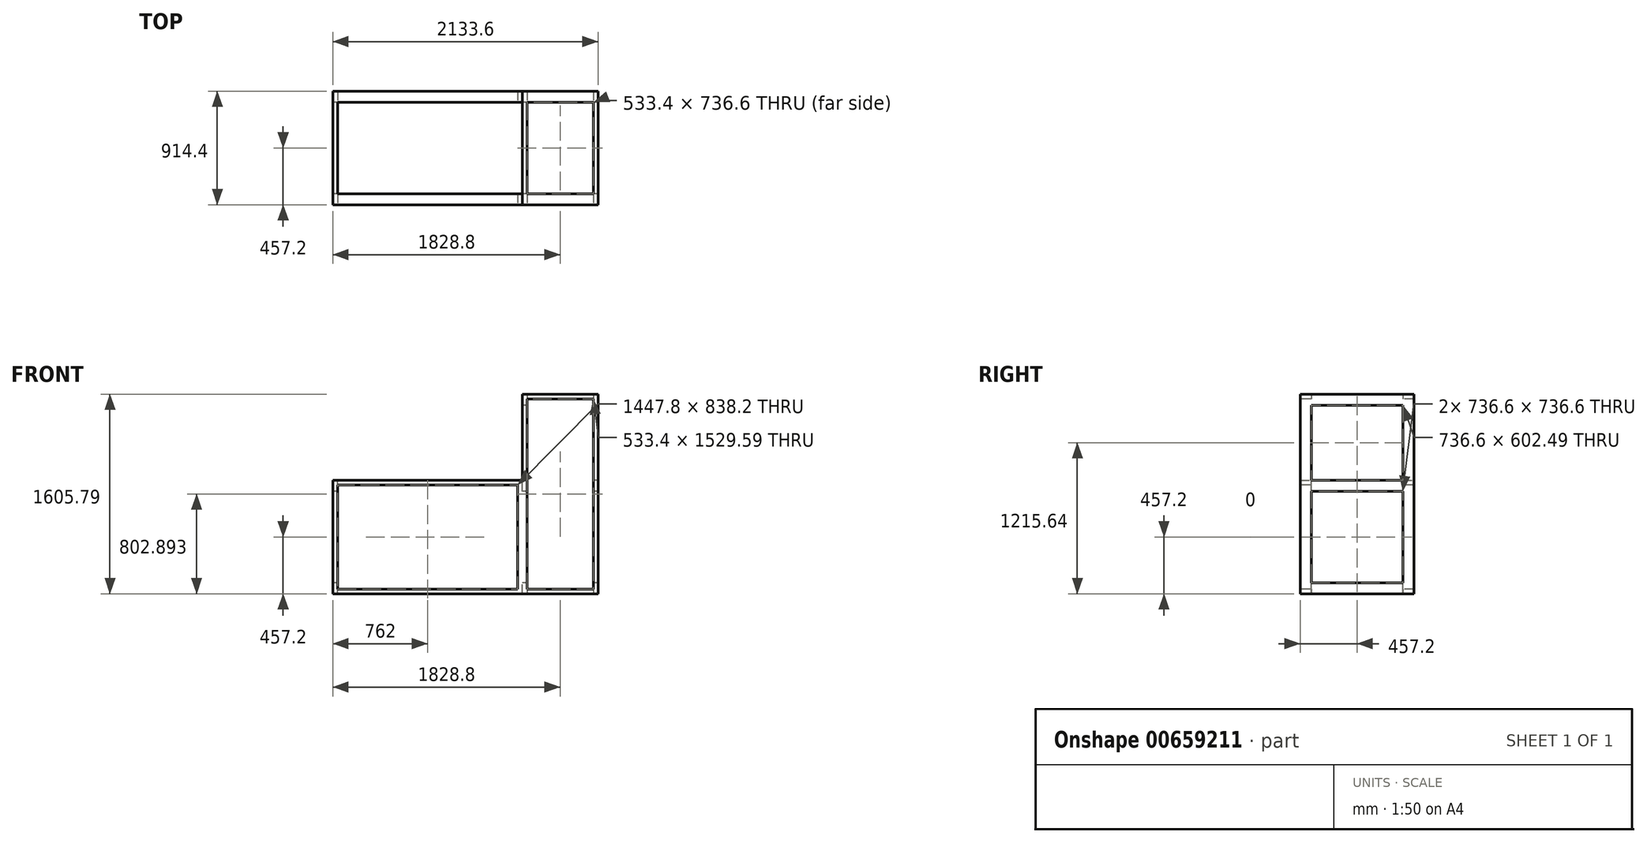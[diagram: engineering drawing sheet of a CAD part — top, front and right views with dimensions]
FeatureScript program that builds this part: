
annotation { "Feature Type Name" : "Feature", "Feature Type Description" : "" }
export const myFeature = defineFeature(function(context is Context, id is Id, definition is map)
    precondition{}
    {
        {
            var Q0;
            Q0=qCreatedBy(makeId("Front.planeOp"),FACE);
            var sketch = newSketch(context, id + "F0", { "sketchPlane" : qUnion([Q0])});
            skLineSegment(sketch, "E0.bottom", {"start": v(762, 457.2) * mm, "end": v(-762, 457.2) * mm});
            skLineSegment(sketch, "E0.top", {"start": v(762, -457.2) * mm, "end": v(-762, -457.2) * mm});
            skLineSegment(sketch, "E0.left", {"start": v(762, 457.2) * mm, "end": v(762, -457.2) * mm});
            skLineSegment(sketch, "E0.right", {"start": v(-762, 457.2) * mm, "end": v(-762, -457.2) * mm});
            skPoint(sketch, "E0.middle", {"position": v(0, 0) * mm});
            skLineSegment(sketch, "E1.bottom", {"start": v(762, -457.2) * mm, "end": v(1371.6, -457.2) * mm});
            skLineSegment(sketch, "E1.top", {"start": v(762, 1148.59) * mm, "end": v(1371.6, 1148.59) * mm});
            skLineSegment(sketch, "E1.left", {"start": v(762, -457.2) * mm, "end": v(762, 1148.59) * mm});
            skLineSegment(sketch, "E1.right", {"start": v(1371.6, -457.2) * mm, "end": v(1371.6, 1148.59) * mm});
            skSolve(sketch);
        }
        {
            var Q0;
            Q0 = qSketchRegion(id + "F0", true);
            extrude(context, id + "F1", {"entities" : qUnion([Q0]), "endBound" : BoundingType.SYMMETRIC, "depth" : 914.4 * mm, "offsetDistance" : 25.4 * mm});
        }
        {
            var Q0;
            Q0=makeQuery(id+"F1.opExtrude","SWEPT_FACE",FACE,{"disambiguationData":[OSD([sQuery(id+"F0.wireOp",EDGE,"E0.right")])]});
            var sketch = newSketch(context, id + "F2", { "sketchPlane" : qUnion([Q0])});
            skLineSegment(sketch, "E2.bottom", {"start": v(368.3, 368.3) * mm, "end": v(-368.3, 368.3) * mm});
            skLineSegment(sketch, "E2.top", {"start": v(368.3, -368.3) * mm, "end": v(-368.3, -368.3) * mm});
            skLineSegment(sketch, "E2.left", {"start": v(368.3, 368.3) * mm, "end": v(368.3, -368.3) * mm});
            skLineSegment(sketch, "E2.right", {"start": v(-368.3, 368.3) * mm, "end": v(-368.3, -368.3) * mm});
            skPoint(sketch, "E2.middle", {"position": v(0, 0) * mm});
            skSolve(sketch);
        }
        {
            var Q0;
            Q0 = qSketchRegion(id + "F2", true);
            extrude(context, id + "F3", {"entities" : qUnion([Q0]), "operationType" : NewBodyOperationType.REMOVE, "endBound" : BoundingType.UP_TO_NEXT, "oppositeDirection" : true, "depth" : 25.4 * mm, "offsetDistance" : 25.4 * mm});
        }
        {
            var Q0;
            Q0=makeQuery(id+"F1.opExtrude","CAP_FACE",FACE,{"disambiguationData":[OSD([sQuery(id+"F0.wireOp",EDGE,"E0.bottom"),sQuery(id+"F0.wireOp",EDGE,"E0.top"),sQuery(id+"F0.wireOp",EDGE,"E0.right"),sQuery(id+"F0.wireOp",EDGE,"E1.bottom"),sQuery(id+"F0.wireOp",EDGE,"E1.top"),sQuery(id+"F0.wireOp",EDGE,"E1.left"),sQuery(id+"F0.wireOp",EDGE,"E1.right")])],"isStart":false});
            var sketch = newSketch(context, id + "F4", { "sketchPlane" : qUnion([Q0])});
            skLineSegment(sketch, "E3.bottom", {"start": v(723.9, 419.1) * mm, "end": v(-723.9, 419.1) * mm});
            skLineSegment(sketch, "E3.top", {"start": v(723.9, -419.1) * mm, "end": v(-723.9, -419.1) * mm});
            skLineSegment(sketch, "E3.left", {"start": v(723.9, 419.1) * mm, "end": v(723.9, -419.1) * mm});
            skLineSegment(sketch, "E3.right", {"start": v(-723.9, 419.1) * mm, "end": v(-723.9, -419.1) * mm});
            skPoint(sketch, "E3.middle", {"position": v(0, 0) * mm});
            skLineSegment(sketch, "E4.bottom", {"start": v(1333.5, 1110.49) * mm, "end": v(800.1, 1110.49) * mm});
            skLineSegment(sketch, "E4.top", {"start": v(1333.5, -419.1) * mm, "end": v(800.1, -419.1) * mm});
            skLineSegment(sketch, "E4.left", {"start": v(1333.5, 1110.49) * mm, "end": v(1333.5, -419.1) * mm});
            skLineSegment(sketch, "E4.right", {"start": v(800.1, 1110.49) * mm, "end": v(800.1, -419.1) * mm});
            skPoint(sketch, "E4.middle", {"position": v(1066.8, 345.7) * mm});
            skSolve(sketch);
        }
        {
            var Q0;
            Q0 = qSketchRegion(id + "F4", true);
            var Q1;
            Q1=makeQuery(id+"F1.opExtrude","CAP_FACE",FACE,{"disambiguationData":[OSD([sQuery(id+"F0.wireOp",EDGE,"E0.bottom"),sQuery(id+"F0.wireOp",EDGE,"E0.top"),sQuery(id+"F0.wireOp",EDGE,"E0.right"),sQuery(id+"F0.wireOp",EDGE,"E1.bottom"),sQuery(id+"F0.wireOp",EDGE,"E1.top"),sQuery(id+"F0.wireOp",EDGE,"E1.left"),sQuery(id+"F0.wireOp",EDGE,"E1.right")])],"isStart":true});
            extrude(context, id + "F5", {"entities" : qUnion([Q0]), "operationType" : NewBodyOperationType.REMOVE, "endBound" : BoundingType.UP_TO_SURFACE, "oppositeDirection" : true, "depth" : 25.4 * mm, "endBoundEntityFace" : qUnion([Q1]), "offsetDistance" : 25.4 * mm});
        }
        {
            var Q0;
            Q0=makeQuery(id+"F1.opExtrude","SWEPT_FACE",FACE,{"disambiguationData":[OSD([sQuery(id+"F0.wireOp",EDGE,"E1.left")])]});
            var sketch = newSketch(context, id + "F6", { "sketchPlane" : qUnion([Q0])});
            skLineSegment(sketch, "E5.bottom", {"start": v(368.3, 1059.69) * mm, "end": v(-368.3, 1059.69) * mm});
            skLineSegment(sketch, "E5.top", {"start": v(368.3, 457.2) * mm, "end": v(-368.3, 457.2) * mm});
            skLineSegment(sketch, "E5.left", {"start": v(368.3, 1059.69) * mm, "end": v(368.3, 457.2) * mm});
            skLineSegment(sketch, "E5.right", {"start": v(-368.3, 1059.69) * mm, "end": v(-368.3, 457.2) * mm});
            skPoint(sketch, "E5.middle", {"position": v(0, 758.44) * mm});
            skSolve(sketch);
        }
        {
            var Q0;
            Q0 = qSketchRegion(id + "F6", true);
            var Q1;
            Q1=makeQuery(id+"F1.opExtrude","SWEPT_FACE",FACE,{"disambiguationData":[OSD([sQuery(id+"F0.wireOp",EDGE,"E1.right")])]});
            extrude(context, id + "F7", {"entities" : qUnion([Q0]), "operationType" : NewBodyOperationType.REMOVE, "endBound" : BoundingType.UP_TO_SURFACE, "oppositeDirection" : true, "depth" : 25.4 * mm, "endBoundEntityFace" : qUnion([Q1]), "offsetDistance" : 25.4 * mm});
        }
        {
            var Q0;
            Q0=makeQuery(id+"F7.boolean.opBoolean","MERGE",FACE,{"derivedFrom":[makeQuery(id+"F1.opExtrude","SWEPT_FACE",FACE,{"disambiguationData":[OSD([sQuery(id+"F0.wireOp",EDGE,"E0.bottom")])]}),makeQuery(id+"F7.opExtrude","SWEPT_FACE",FACE,{"disambiguationData":[OSD([sQuery(id+"F6.wireOp",EDGE,"E5.top")])]})]});
            var sketch = newSketch(context, id + "F8", { "sketchPlane" : qUnion([Q0])});
            skPoint(sketch, "E6.middle", {"position": v(0, 0) * mm});
            skLineSegment(sketch, "E7.bottom", {"start": v(762, -368.3) * mm, "end": v(-723.9, -368.3) * mm});
            skLineSegment(sketch, "E7.top", {"start": v(762, 368.3) * mm, "end": v(-723.9, 368.3) * mm});
            skLineSegment(sketch, "E7.left", {"start": v(762, -368.3) * mm, "end": v(762, 368.3) * mm});
            skLineSegment(sketch, "E7.right", {"start": v(-723.9, -368.3) * mm, "end": v(-723.9, 368.3) * mm});
            skSolve(sketch);
        }
        {
            var Q0;
            Q0 = qSketchRegion(id + "F8", true);
            var Q1;
            Q1=makeQuery(id+"F1.opExtrude","SWEPT_FACE",FACE,{"disambiguationData":[OSD([sQuery(id+"F0.wireOp",EDGE,"E0.top"),sQuery(id+"F0.wireOp",EDGE,"E1.bottom")])]});
            extrude(context, id + "F9", {"entities" : qUnion([Q0]), "operationType" : NewBodyOperationType.REMOVE, "endBound" : BoundingType.UP_TO_SURFACE, "oppositeDirection" : true, "depth" : 25.4 * mm, "endBoundEntityFace" : qUnion([Q1]), "offsetDistance" : 25.4 * mm});
        }
        {
            var Q0;
            Q0 = qSketchRegion(id + "F8", true);
            var Q1;
            Q1=makeQuery(id+"F1.opExtrude","SWEPT_FACE",FACE,{"disambiguationData":[OSD([sQuery(id+"F0.wireOp",EDGE,"E0.top"),sQuery(id+"F0.wireOp",EDGE,"E1.bottom")])]});
            extrude(context, id + "F10", {"entities" : qUnion([Q0]), "operationType" : NewBodyOperationType.REMOVE, "endBound" : BoundingType.UP_TO_SURFACE, "oppositeDirection" : true, "depth" : 25.4 * mm, "endBoundEntityFace" : qUnion([Q1]), "offsetDistance" : 25.4 * mm});
        }
        {
            var Q0;
            Q0=makeQuery(id+"F1.opExtrude","SWEPT_FACE",FACE,{"disambiguationData":[OSD([sQuery(id+"F0.wireOp",EDGE,"E0.top"),sQuery(id+"F0.wireOp",EDGE,"E1.bottom")])]});
            var sketch = newSketch(context, id + "F11", { "sketchPlane" : qUnion([Q0])});
            skLineSegment(sketch, "E8.bottom", {"start": v(800.1, -368.3) * mm, "end": v(1333.5, -368.3) * mm});
            skLineSegment(sketch, "E8.top", {"start": v(800.1, 368.3) * mm, "end": v(1333.5, 368.3) * mm});
            skLineSegment(sketch, "E8.left", {"start": v(800.1, -368.3) * mm, "end": v(800.1, 368.3) * mm});
            skLineSegment(sketch, "E8.right", {"start": v(1333.5, -368.3) * mm, "end": v(1333.5, 368.3) * mm});
            skPoint(sketch, "E8.middle", {"position": v(1066.8, 0) * mm});
            skSolve(sketch);
        }
        {
            var Q0;
            Q0 = qSketchRegion(id + "F11", true);
            var Q1;
            Q1=makeQuery(id+"F1.opExtrude","SWEPT_FACE",FACE,{"disambiguationData":[OSD([sQuery(id+"F0.wireOp",EDGE,"E1.top")])]});
            extrude(context, id + "F12", {"entities" : qUnion([Q0]), "operationType" : NewBodyOperationType.REMOVE, "endBound" : BoundingType.UP_TO_SURFACE, "oppositeDirection" : true, "depth" : 25.4 * mm, "endBoundEntityFace" : qUnion([Q1]), "offsetDistance" : 25.4 * mm});
        }
    });
